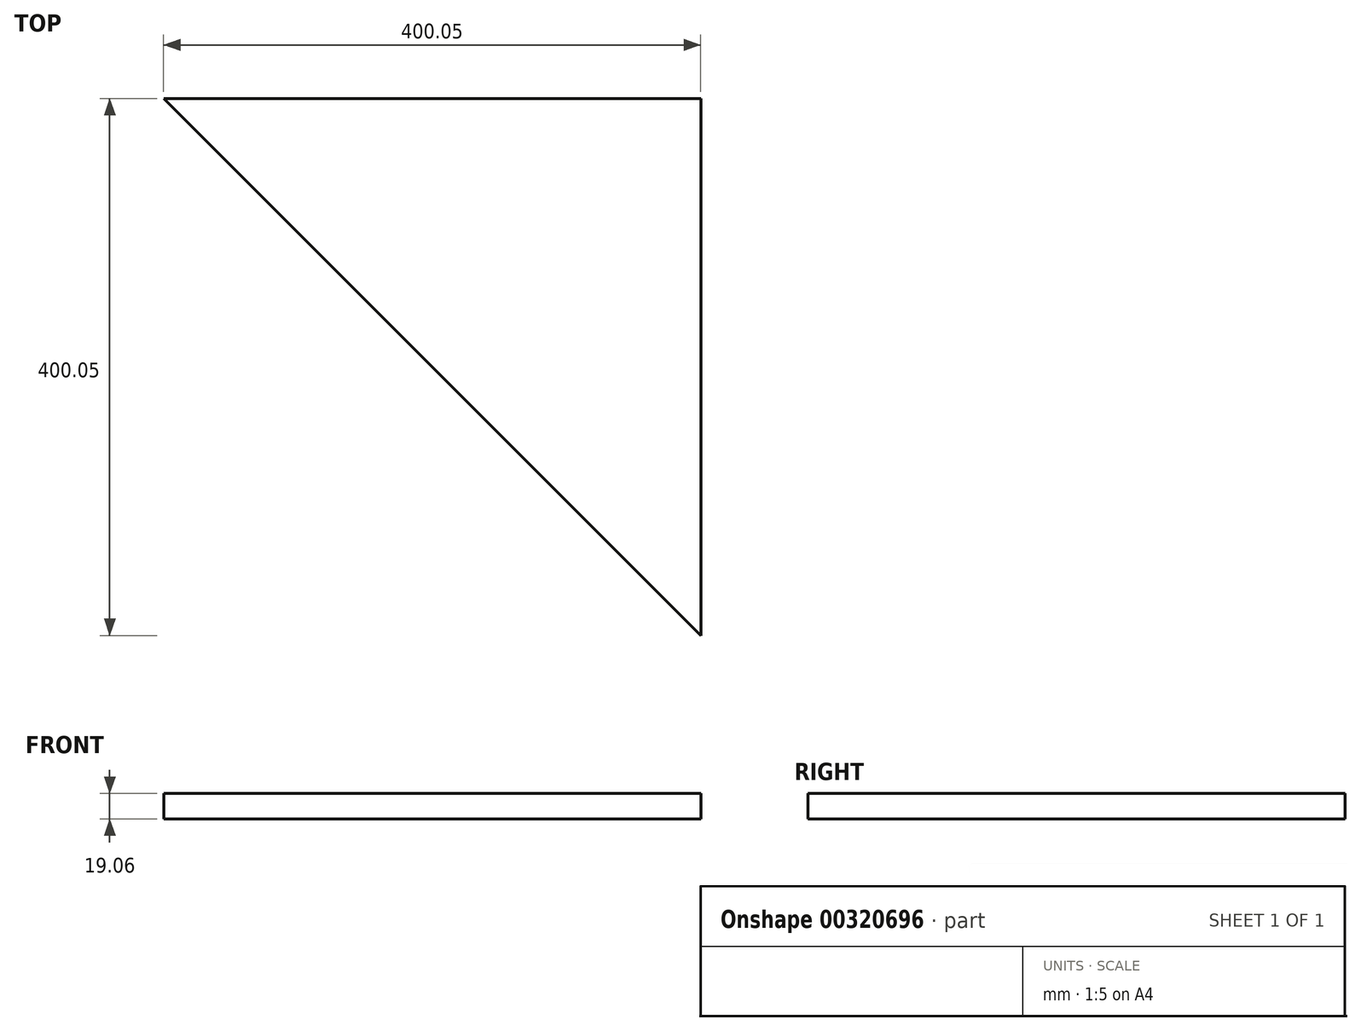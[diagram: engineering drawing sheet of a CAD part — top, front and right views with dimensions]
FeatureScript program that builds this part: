
annotation { "Feature Type Name" : "Feature", "Feature Type Description" : "" }
export const myFeature = defineFeature(function(context is Context, id is Id, definition is map)
    precondition{}
    {
        {
            var Q0;
            Q0=qCreatedBy(makeId("Top.planeOp"),FACE);
            var sketch = newSketch(context, id + "F0", { "sketchPlane" : qUnion([Q0])});
            skLineSegment(sketch, "E0", {"start": v(40.34, -208.34) * mm, "end": v(40.34, 191.7) * mm});
            skLineSegment(sketch, "E1", {"start": v(40.34, 191.7) * mm, "end": v(-359.7, 191.7) * mm});
            skLineSegment(sketch, "E2", {"start": v(-359.7, 191.7) * mm, "end": v(40.34, -208.34) * mm});
            skSolve(sketch);
        }
        {
            var Q0;
            Q0 = qSketchRegion(id + "F0", true);
            extrude(context, id + "F1", {"entities" : qUnion([Q0]), "depth" : 19.05 * mm, "symmetric" : true});
        }
    });
